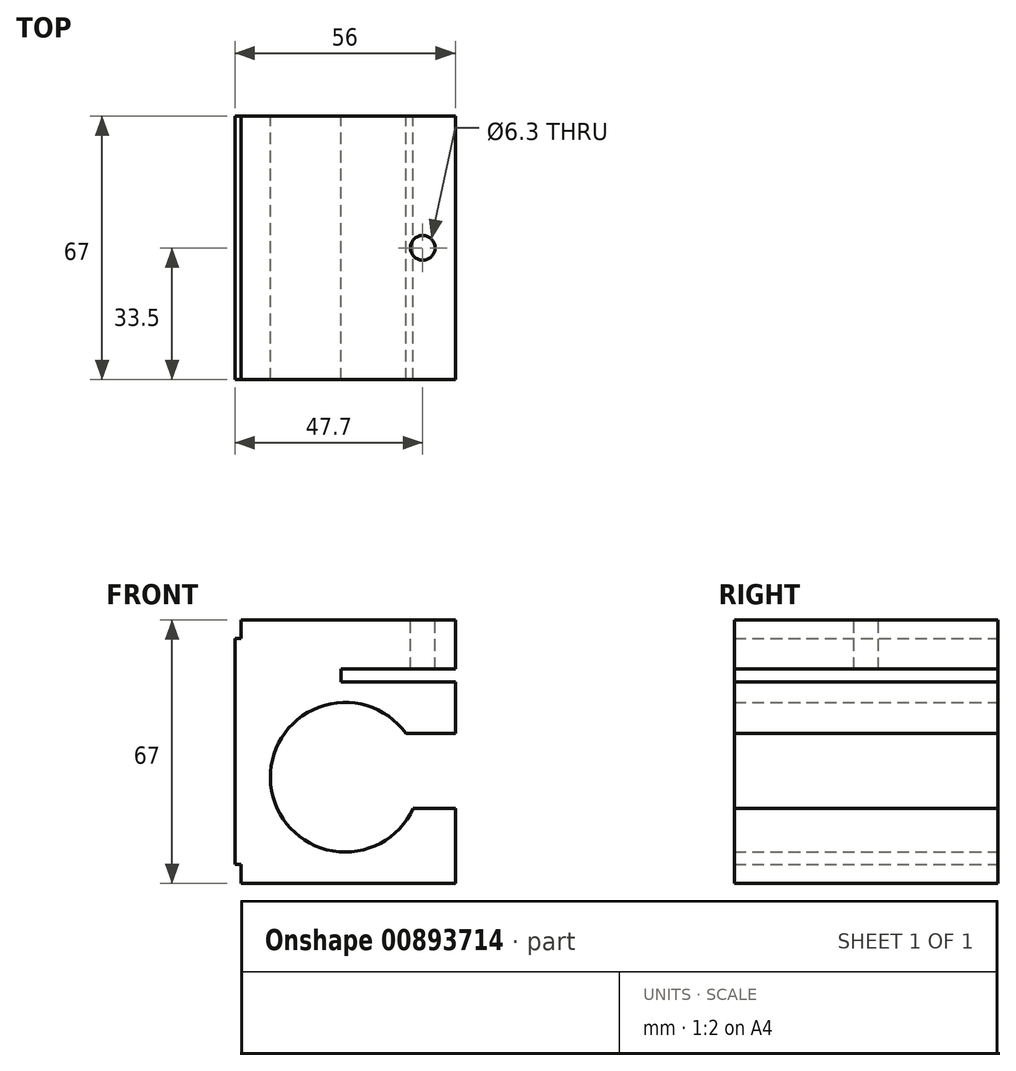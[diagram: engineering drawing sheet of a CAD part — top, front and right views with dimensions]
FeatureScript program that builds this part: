
annotation { "Feature Type Name" : "Feature", "Feature Type Description" : "" }
export const myFeature = defineFeature(function(context is Context, id is Id, definition is map)
    precondition{}
    {
        {
            var Q0;
            Q0=qCreatedBy(makeId("Front.planeOp"),FACE);
            var sketch = newSketch(context, id + "F0", { "sketchPlane" : qUnion([Q0])});
            skLineSegment(sketch, "E0.bottom", {"start": v(28, -33.5) * mm, "end": v(-26.5, -33.5) * mm});
            skLineSegment(sketch, "E0.top", {"start": v(28, 33.5) * mm, "end": v(-26.5, 33.5) * mm});
            skLineSegment(sketch, "E0.left", {"start": v(28, -33.5) * mm, "end": v(28, -14.39) * mm});
            skLineSegment(sketch, "E0.right", {"start": v(-28, -28.7) * mm, "end": v(-28, 28.7) * mm});
            skPoint(sketch, "E0.middle", {"position": v(0, 0) * mm});
            skLineSegment(sketch, "E1", {"start": v(28, 21) * mm, "end": v(-1, 21) * mm});
            skLineSegment(sketch, "E2", {"start": v(-1, 21) * mm, "end": v(-1, 17.7) * mm});
            skLineSegment(sketch, "E3", {"start": v(-1, 17.7) * mm, "end": v(28, 17.7) * mm});
            skLineSegment(sketch, "E4.trimOffspring", {"start": v(28, 21) * mm, "end": v(28, 33.5) * mm});
            skArc(sketch, "E5", {"start": v(15.41, 4.61) * mm, "mid": v(-18.9, -8.37) * mm, "end": v(17.29, -14.39) * mm});
            skLineSegment(sketch, "E6", {"start": v(15.41, 4.61) * mm, "end": v(28, 4.61) * mm});
            skLineSegment(sketch, "E7", {"start": v(17.29, -14.39) * mm, "end": v(28, -14.39) * mm});
            skLineSegment(sketch, "E8", {"start": v(-28, -28.7) * mm, "end": v(-26.5, -28.7) * mm});
            skLineSegment(sketch, "E9", {"start": v(-26.5, -28.7) * mm, "end": v(-26.5, -33.5) * mm});
            skLineSegment(sketch, "E10", {"start": v(-26.5, 33.5) * mm, "end": v(-26.5, 28.7) * mm});
            skLineSegment(sketch, "E11", {"start": v(-26.5, 28.7) * mm, "end": v(-28, 28.7) * mm});
            skPoint(sketch, "E12.orphan", {"position": v(-28, 33.5) * mm});
            skPoint(sketch, "E13.orphan", {"position": v(-28, -33.5) * mm});
            skLineSegment(sketch, "E14.trimOffspring", {"start": v(28, 4.61) * mm, "end": v(28, 17.7) * mm});
            skSolve(sketch);
        }
        {
            var Q0;
            Q0=makeQuery(id+"F0.imprint","IMPRINT",FACE,{"disambiguationData":[TD([[makeQuery(id+"F0.imprint","IMPRINT",EDGE,{"derivedFrom":sQuery(id+"F0.wireOp",EDGE,"E0.bottom")}),-1.0]])]});
            extrude(context, id + "F1", {"entities" : qUnion([Q0]), "depth" : 67 * mm, "offsetDistance" : 25.4 * mm});
        }
        {
            var Q0;
            Q0=makeQuery(id+"F1.opExtrude","SWEPT_FACE",FACE,{"disambiguationData":[OSD([sQuery(id+"F0.wireOp",EDGE,"E0.top")])]});
            var sketch = newSketch(context, id + "F2", { "sketchPlane" : qUnion([Q0])});
            skCircle(sketch, "E15", {"center": v(19.7, -33.5) * mm, "radius": 3.15 * mm});
            skSolve(sketch);
        }
        {
            var Q0;
            Q0 = qSketchRegion(id + "F2", true);
            extrude(context, id + "F3", {"entities" : qUnion([Q0]), "operationType" : NewBodyOperationType.REMOVE, "oppositeDirection" : true, "depth" : 12.5 * mm, "offsetDistance" : 25.4 * mm});
        }
    });
